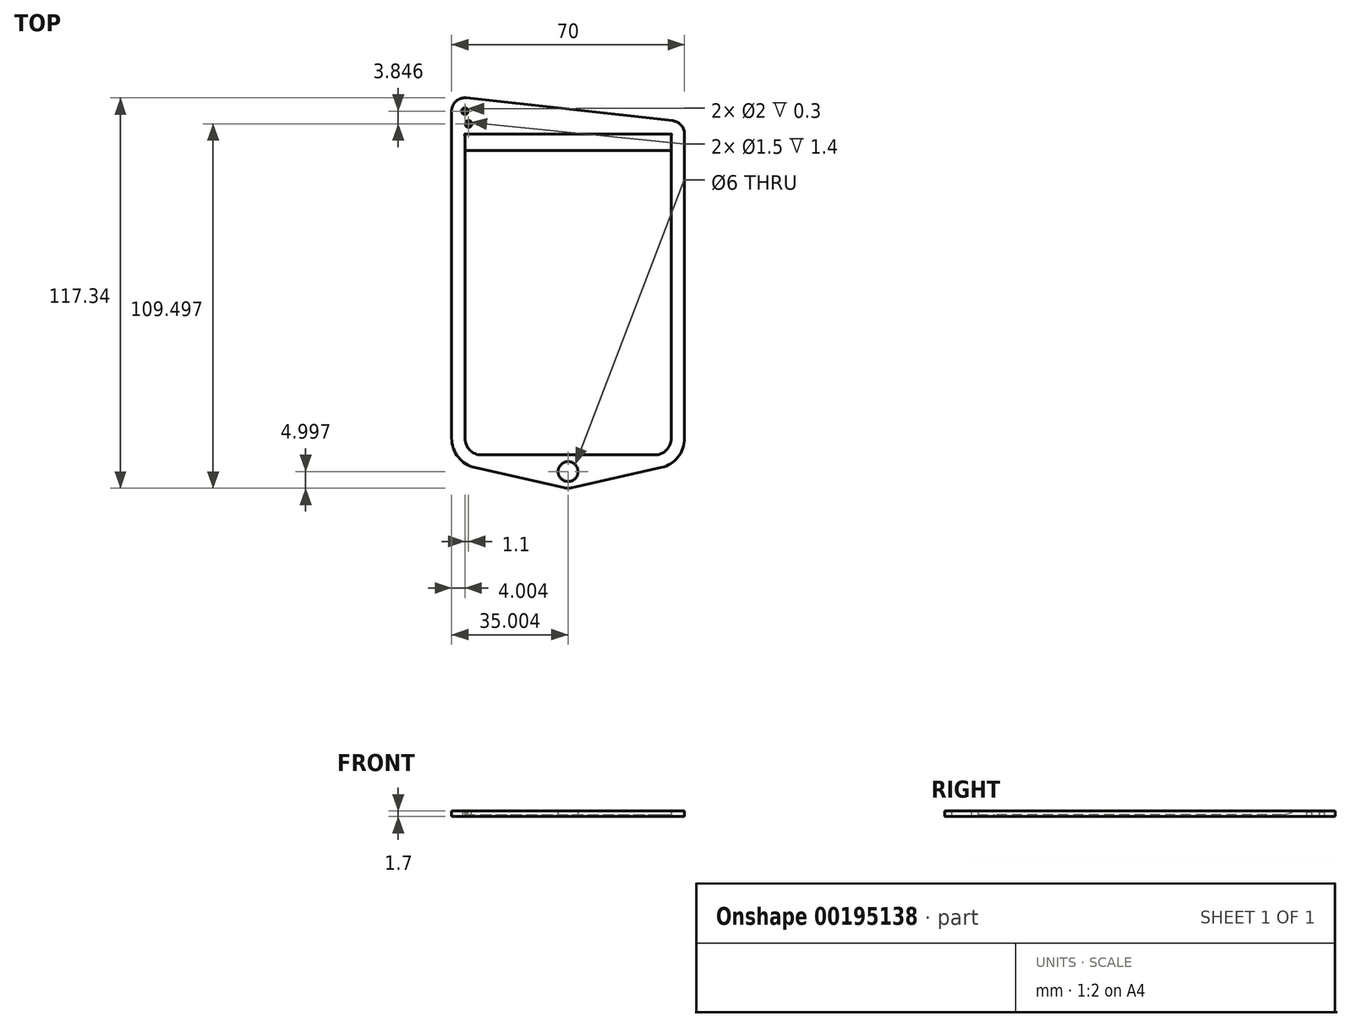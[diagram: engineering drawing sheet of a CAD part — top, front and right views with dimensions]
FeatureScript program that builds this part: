
annotation { "Feature Type Name" : "Feature", "Feature Type Description" : "" }
export const myFeature = defineFeature(function(context is Context, id is Id, definition is map)
    precondition{}
    {
        {
            assignVariable(context, id + "F0", {"name" : "ccthickness", "anyValue" : 1});
        }
        {
            assignVariable(context, id + "F1", {"name" : "backplate", "anyValue" : 0.5});
        }
        {
            assignVariable(context, id + "F2", {"name" : "platethickness", "anyValue" : (getVariable(context, 'ccthickness') + getVariable(context, 'backplate') + 0.2)});
        }
        {
            var Q0;
            Q0=qCreatedBy(makeId("Top.planeOp"),FACE);
            var sketch = newSketch(context, id + "F3", { "sketchPlane" : qUnion([Q0])});
            skLineSegment(sketch, "E0.bottom", {"start": v(-38.74, 72.64) * mm, "end": v(13.26, 72.64) * mm, "construction": true});
            skLineSegment(sketch, "E0.top", {"start": v(-38.74, -17.36) * mm, "end": v(13.26, -17.36) * mm, "construction": true});
            skLineSegment(sketch, "E0.left", {"start": v(-42.74, 68.64) * mm, "end": v(-42.74, -13.36) * mm, "construction": true});
            skLineSegment(sketch, "E0.right", {"start": v(17.26, 68.64) * mm, "end": v(17.26, -13.36) * mm, "construction": true});
            skArc(sketch, "E1.filletArc", {"start": v(-38.74, 72.64) * mm, "mid": v(-41.56, 71.46) * mm, "end": v(-42.74, 68.64) * mm, "construction": true});
            skArc(sketch, "E2.filletArc", {"start": v(17.26, 68.64) * mm, "mid": v(16.1, 71.46) * mm, "end": v(13.26, 72.64) * mm, "construction": true});
            skArc(sketch, "E3.filletArc", {"start": v(13.26, -17.36) * mm, "mid": v(16.1, -16.2) * mm, "end": v(17.26, -13.36) * mm, "construction": true});
            skArc(sketch, "E4.filletArc", {"start": v(-42.74, -13.36) * mm, "mid": v(-41.56, -16.2) * mm, "end": v(-38.74, -17.36) * mm, "construction": true});
            skSolve(sketch);
        }
        {
            var Q0;
            Q0=qCreatedBy(makeId("Top.planeOp"),FACE);
            var sketch = newSketch(context, id + "F4", { "sketchPlane" : qUnion([Q0])});
            skLineSegment(sketch, "E5.0", {"start": v(-38.74, 72.64) * mm, "end": v(13.26, 72.64) * mm, "construction": true});
            skArc(sketch, "E5.1", {"start": v(17.26, 68.64) * mm, "mid": v(16.1, 71.46) * mm, "end": v(13.26, 72.64) * mm, "construction": true});
            skLineSegment(sketch, "E5.2", {"start": v(17.26, 68.64) * mm, "end": v(17.26, -13.36) * mm, "construction": true});
            skLineSegment(sketch, "E5.3", {"start": v(-42.74, 68.64) * mm, "end": v(-42.74, -13.36) * mm, "construction": true});
            skArc(sketch, "E5.4", {"start": v(-38.74, 72.64) * mm, "mid": v(-41.56, 71.46) * mm, "end": v(-42.74, 68.64) * mm, "construction": true});
            skArc(sketch, "E5.5", {"start": v(-42.74, -13.36) * mm, "mid": v(-41.56, -16.2) * mm, "end": v(-38.74, -17.36) * mm, "construction": true});
            skLineSegment(sketch, "E5.6", {"start": v(-38.74, -17.36) * mm, "end": v(13.26, -17.36) * mm, "construction": true});
            skLineSegment(sketch, "E6.bottom", {"start": v(-43.74, 78.14) * mm, "end": v(18.26, 78.14) * mm});
            skLineSegment(sketch, "E6.top", {"start": v(-38.74, -18.36) * mm, "end": v(13.26, -18.36) * mm});
            skLineSegment(sketch, "E6.left", {"start": v(-43.74, 78.14) * mm, "end": v(-43.74, -13.36) * mm});
            skLineSegment(sketch, "E6.right", {"start": v(18.26, 78.14) * mm, "end": v(18.26, -13.36) * mm});
            skLineSegment(sketch, "E7", {"start": v(-43.74, 73.14) * mm, "end": v(18.26, 73.14) * mm});
            skPoint(sketch, "E8.visualSharp", {"position": v(-43.74, -18.36) * mm});
            skArc(sketch, "E8.filletArc", {"start": v(-43.74, -13.36) * mm, "mid": v(-42.27, -16.9) * mm, "end": v(-38.74, -18.36) * mm});
            skPoint(sketch, "E9.visualSharp", {"position": v(18.26, -18.36) * mm});
            skArc(sketch, "E9.filletArc", {"start": v(13.26, -18.36) * mm, "mid": v(16.8, -16.9) * mm, "end": v(18.26, -13.36) * mm});
            skLineSegment(sketch, "E10.top", {"start": v(-38.74, -22.36) * mm, "end": v(13.26, -22.36) * mm, "construction": true});
            skLineSegment(sketch, "E10.left", {"start": v(-47.74, 84.98) * mm, "end": v(-47.74, -13.36) * mm});
            skLineSegment(sketch, "E10.right", {"start": v(22.26, 78.14) * mm, "end": v(22.26, -13.36) * mm});
            skPoint(sketch, "E11.visualSharp", {"position": v(-47.74, -22.36) * mm});
            skPoint(sketch, "E12.visualSharp", {"position": v(22.26, -22.36) * mm});
            skPoint(sketch, "E13.visualSharp", {"position": v(22.26, 82.14) * mm});
            skArc(sketch, "E13.filletArc", {"start": v(22.26, 78.14) * mm, "mid": v(21.24, 80.8) * mm, "end": v(18.7, 82.11) * mm});
            skLineSegment(sketch, "E14", {"start": v(-12.74, -18.36) * mm, "end": v(-12.74, -28.36) * mm, "construction": true});
            skCircle(sketch, "E15", {"center": v(-12.74, -23.36) * mm, "radius": 3 * mm});
            skArc(sketch, "E16.filletArc", {"start": v(-47.74, -13.36) * mm, "mid": v(-45.77, -18.98) * mm, "end": v(-40.73, -22.14) * mm});
            skArc(sketch, "E17.filletArc", {"start": v(13.26, -22.36) * mm, "mid": v(14.27, -22.3) * mm, "end": v(15.26, -22.14) * mm, "construction": true});
            skLineSegment(sketch, "E18", {"start": v(-40.73, -22.14) * mm, "end": v(-13.84, -28.24) * mm});
            skLineSegment(sketch, "E19", {"start": v(-11.63, -28.24) * mm, "end": v(15.26, -22.14) * mm});
            skArc(sketch, "E20", {"start": v(-40.73, -22.14) * mm, "mid": v(-39.74, -22.3) * mm, "end": v(-38.74, -22.36) * mm, "construction": true});
            skArc(sketch, "E21", {"start": v(15.26, -22.14) * mm, "mid": v(20.3, -18.98) * mm, "end": v(22.26, -13.36) * mm});
            skArc(sketch, "E22", {"start": v(-13.84, -28.24) * mm, "mid": v(-12.74, -28.36) * mm, "end": v(-11.63, -28.24) * mm});
            skArc(sketch, "E23", {"start": v(-11.63, -28.24) * mm, "mid": v(-12.74, -18.36) * mm, "end": v(-13.84, -28.24) * mm, "construction": true});
            skLineSegment(sketch, "E24", {"start": v(-12.74, -23.36) * mm, "end": v(-42.64, 81.14) * mm, "construction": true});
            skCircle(sketch, "E25", {"center": v(-42.64, 81.14) * mm, "radius": 1 * mm});
            skCircle(sketch, "E26", {"center": v(-42.64, 81.14) * mm, "radius": 0.75 * mm});
            skLineSegment(sketch, "E27", {"start": v(-42.64, 81.14) * mm, "end": v(-43.74, 84.98) * mm, "construction": true});
            skCircle(sketch, "E28", {"center": v(-43.74, 84.98) * mm, "radius": 0.75 * mm});
            skCircle(sketch, "E29", {"center": v(-43.74, 84.98) * mm, "radius": 1 * mm});
            skLineSegment(sketch, "E30", {"start": v(-43.74, 78.14) * mm, "end": v(-43.74, 87.36) * mm, "construction": true});
            skLineSegment(sketch, "E31", {"start": v(-43.3, 88.96) * mm, "end": v(18.7, 82.11) * mm});
            skLineSegment(sketch, "E32", {"start": v(18.26, 78.14) * mm, "end": v(18.26, 82.14) * mm, "construction": true});
            skArc(sketch, "E33", {"start": v(18.7, 82.11) * mm, "mid": v(18.48, 82.13) * mm, "end": v(18.26, 82.14) * mm, "construction": true});
            skArc(sketch, "E34", {"start": v(-43.3, 88.96) * mm, "mid": v(-46.4, 87.96) * mm, "end": v(-47.74, 84.98) * mm});
            skArc(sketch, "E35", {"start": v(-47.74, 84.98) * mm, "mid": v(-41.07, 82) * mm, "end": v(-43.3, 88.96) * mm, "construction": true});
            skSolve(sketch);
        }
        {
            var Q0;
            {var subQ5=sQuery(id+"F4.wireOp",EDGE,"E6.bottom");Q0=makeQuery(id+"F4.imprint","IMPRINT",FACE,{"disambiguationData":[TD([[makeQuery(id+"F4.imprint","IMPRINT",EDGE,{"derivedFrom":subQ5}),1.0]])]});}
            extrude(context, id + "F5", {"entities" : qUnion([Q0]), "depth" : (getVariable(context, 'platethickness')) * mm, "offsetDistance" : 25 * mm});
        }
        {
            var Q0;
            Q0=makeQuery(id+"F4.imprint","IMPRINT",FACE,{"disambiguationData":[TD([[makeQuery(id+"F4.imprint","IMPRINT",EDGE,{"derivedFrom":sQuery(id+"F4.wireOp",EDGE,"E6.top")}),1.0]])]});
            extrude(context, id + "F6", {"entities" : qUnion([Q0]), "operationType" : NewBodyOperationType.ADD, "depth" : (getVariable(context, 'backplate')) * mm, "offsetDistance" : 25 * mm});
        }
        {
            var Q0;
            Q0=makeQuery(id+"F5.opExtrude","SWEPT_FACE",FACE,{"disambiguationData":[OSD([sQuery(id+"F4.wireOp",EDGE,"E6.right")])]});
            var sketch = newSketch(context, id + "F7", { "sketchPlane" : qUnion([Q0])});
            skLineSegment(sketch, "E36.0", {"start": v(-73.14, 0.5) * mm, "end": v(-73.14, 0) * mm});
            skLineSegment(sketch, "E36.1", {"start": v(-78.14, 1.7) * mm, "end": v(-78.14, 0) * mm});
            skLineSegment(sketch, "E37", {"start": v(-78.14, 0) * mm, "end": v(-78.14, 1.7) * mm});
            skLineSegment(sketch, "E38", {"start": v(-78.14, 1.7) * mm, "end": v(-73.14, 0.5) * mm});
            skLineSegment(sketch, "E39", {"start": v(-73.14, 0) * mm, "end": v(-78.14, 0) * mm});
            skSolve(sketch);
        }
        {
            var Q0;
            Q0=makeQuery(id+"F7.imprint","IMPRINT",FACE,{"disambiguationData":[TD([[makeQuery(id+"F7.imprint","IMPRINT",EDGE,{"derivedFrom":sQuery(id+"F7.wireOp",EDGE,"E36.0")}),-1.0]])]});
            extrude(context, id + "F8", {"entities" : qUnion([Q0]), "operationType" : NewBodyOperationType.ADD, "endBound" : BoundingType.UP_TO_NEXT, "depth" : 25 * mm, "offsetDistance" : 25 * mm});
        }
        {
            var Q0;
            Q0=makeQuery(id+"F4.imprint","IMPRINT",FACE,{"disambiguationData":[TD([[makeQuery(id+"F4.imprint","IMPRINT",EDGE,{"derivedFrom":sQuery(id+"F4.wireOp",EDGE,"E28")}),-1.0]])]});
            var Q1;
            Q1=makeQuery(id+"F4.imprint","IMPRINT",FACE,{"disambiguationData":[TD([[makeQuery(id+"F4.imprint","IMPRINT",EDGE,{"derivedFrom":sQuery(id+"F4.wireOp",EDGE,"E25")}),1.0]])]});
            var Q2;
            Q2=makeQuery(id+"F5.opExtrude","CAP_FACE",FACE,{"disambiguationData":[OSD([sQuery(id+"F4.wireOp",EDGE,"E6.bottom"),sQuery(id+"F4.wireOp",EDGE,"E6.top"),sQuery(id+"F4.wireOp",EDGE,"E6.left"),sQuery(id+"F4.wireOp",EDGE,"E6.right"),sQuery(id+"F4.wireOp",EDGE,"E8.filletArc"),sQuery(id+"F4.wireOp",EDGE,"E9.filletArc"),sQuery(id+"F4.wireOp",EDGE,"E10.left"),sQuery(id+"F4.wireOp",EDGE,"E10.right"),sQuery(id+"F4.wireOp",EDGE,"E13.filletArc"),sQuery(id+"F4.wireOp",EDGE,"E15"),sQuery(id+"F4.wireOp",EDGE,"E16.filletArc"),sQuery(id+"F4.wireOp",EDGE,"E18"),sQuery(id+"F4.wireOp",EDGE,"E19"),sQuery(id+"F4.wireOp",EDGE,"E21"),sQuery(id+"F4.wireOp",EDGE,"E22"),sQuery(id+"F4.wireOp",EDGE,"E25"),sQuery(id+"F4.wireOp",EDGE,"E29"),sQuery(id+"F4.wireOp",EDGE,"E31"),sQuery(id+"F4.wireOp",EDGE,"E34")])],"isStart":false});
            extrude(context, id + "F9", {"entities" : qUnion([Q0, Q1]), "operationType" : NewBodyOperationType.ADD, "endBound" : BoundingType.UP_TO_SURFACE, "depth" : 25 * mm, "endBoundEntityFace" : qUnion([Q2]), "hasOffset" : true, "offsetDistance" : (getVariable(context, 'platethickness') - (1.6 - 0.2)) * mm});
        }
        {
            var Q0;
            Q0=makeQuery(id+"F5.opExtrude","CAP_EDGE",EDGE,{"disambiguationData":[OSD([sQuery(id+"F4.wireOp",EDGE,"E6.left")])],"isStart":false});
            var Q1;
            Q1=makeQuery(id+"F5.opExtrude","CAP_EDGE",EDGE,{"disambiguationData":[OSD([sQuery(id+"F4.wireOp",EDGE,"E10.right")])],"isStart":false});
            var Q2;
            Q2=makeQuery(id+"F5.opExtrude","CAP_EDGE",EDGE,{"disambiguationData":[OSD([sQuery(id+"F4.wireOp",EDGE,"E18")])],"isStart":true});
            fillet(context, id + "F10", {"entities" : qUnion([Q0, Q1, Q2]), "radius" : 0.25 * mm, "tangentPropagation" : true, "allowEdgeOverflow" : false});
        }
    });
